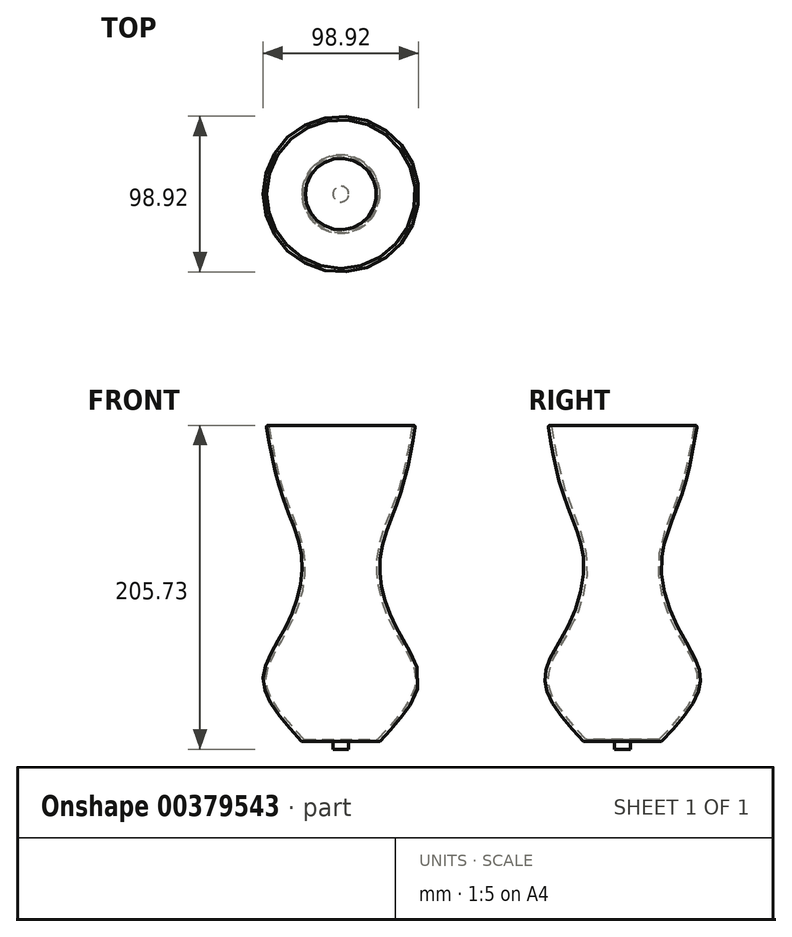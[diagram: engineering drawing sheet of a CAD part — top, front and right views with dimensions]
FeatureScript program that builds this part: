
annotation { "Feature Type Name" : "Feature", "Feature Type Description" : "" }
export const myFeature = defineFeature(function(context is Context, id is Id, definition is map)
    precondition{}
    {
        {
            var Q0;
            Q0=qCreatedBy(makeId("Front.planeOp"),FACE);
            var sketch = newSketch(context, id + "F0", { "sketchPlane" : qUnion([Q0])});
            skLineSegment(sketch, "E0", {"start": v(0, 0) * mm, "end": v(0, 200) * mm, "construction": true});
            skLineSegment(sketch, "E1", {"start": v(0, 0) * mm, "end": v(-24.84, 0) * mm});
            skFitSpline(sketch, "E2", {"points": [v(-24.84, 0) * mm, v(-49.43, 38.31) * mm, v(-34.87, 72.96) * mm, v(-24.84, 116.04) * mm, v(-37.51, 156.48) * mm, v(-47.18, 199.57) * mm], "startDerivative": vector(-173.74, 187.98) * mm, "endDerivative": vector(-36.6, 215.45) * mm});
            skFitSpline(sketch, "E3.0", {"points": [v(-23.37, 1.36) * mm, v(-27, 5.27) * mm, v(-32.4, 11.12) * mm, v(-38.6, 18.8) * mm, v(-42.51, 24.46) * mm, v(-44.97, 29.06) * mm, v(-46.34, 32.66) * mm, v(-47.06, 35.3) * mm, v(-47.39, 37.46) * mm, v(-47.47, 39.16) * mm, v(-47.44, 40.86) * mm, v(-47.2, 43) * mm, v(-46.4, 46.48) * mm, v(-44.75, 50.93) * mm, v(-41.94, 56.46) * mm, v(-39.18, 61.25) * mm, v(-36.88, 65.2) * mm, v(-35.14, 68.23) * mm, v(-33.44, 71.34) * mm, v(-31.82, 74.53) * mm, v(-30.3, 77.78) * mm, v(-28.43, 82.18) * mm, v(-26.38, 87.8) * mm, v(-24.46, 94.67) * mm, v(-23.15, 101.6) * mm, v(-22.63, 107.39) * mm, v(-22.58, 111.99) * mm, v(-22.75, 115.42) * mm, v(-23.12, 118.8) * mm, v(-23.87, 123.26) * mm, v(-25.22, 128.73) * mm, v(-27.31, 135.14) * mm, v(-29.68, 141.47) * mm, v(-32.16, 147.74) * mm, v(-34.16, 152.97) * mm, v(-35.64, 157.16) * mm, v(-37.02, 161.38) * mm, v(-38.56, 166.73) * mm, v(-40.17, 173.24) * mm, v(-41.6, 179.83) * mm, v(-43.3, 188.7) * mm, v(-44.45, 195.41) * mm, v(-45.21, 199.9) * mm]});
            skArc(sketch, "E4", {"start": v(-45.21, 199.9) * mm, "mid": v(-46.36, 200.72) * mm, "end": v(-47.18, 199.57) * mm});
            skLineSegment(sketch, "E5", {"start": v(-23.37, 1.36) * mm, "end": v(0, 1.36) * mm});
            skLineSegment(sketch, "E6", {"start": v(0, 1.36) * mm, "end": v(0, 0) * mm});
            skLineSegment(sketch, "E7", {"start": v(0, 0) * mm, "end": v(0, -5) * mm});
            skLineSegment(sketch, "E8", {"start": v(0, -5) * mm, "end": v(-5, -5) * mm});
            skLineSegment(sketch, "E9", {"start": v(-5, -5) * mm, "end": v(-5, 0) * mm});
            skSolve(sketch);
        }
        {
            var Q0;
            Q0 = qSketchRegion(id + "F0", true);
            var Q1;
            Q1=sQuery(id+"F0.wireOp",EDGE,"E0");
            revolve(context, id + "F1", {"entities" : qUnion([Q0]), "axis" : qUnion([Q1]), "revolveType" : RevolveType.FULL});
        }
    });
